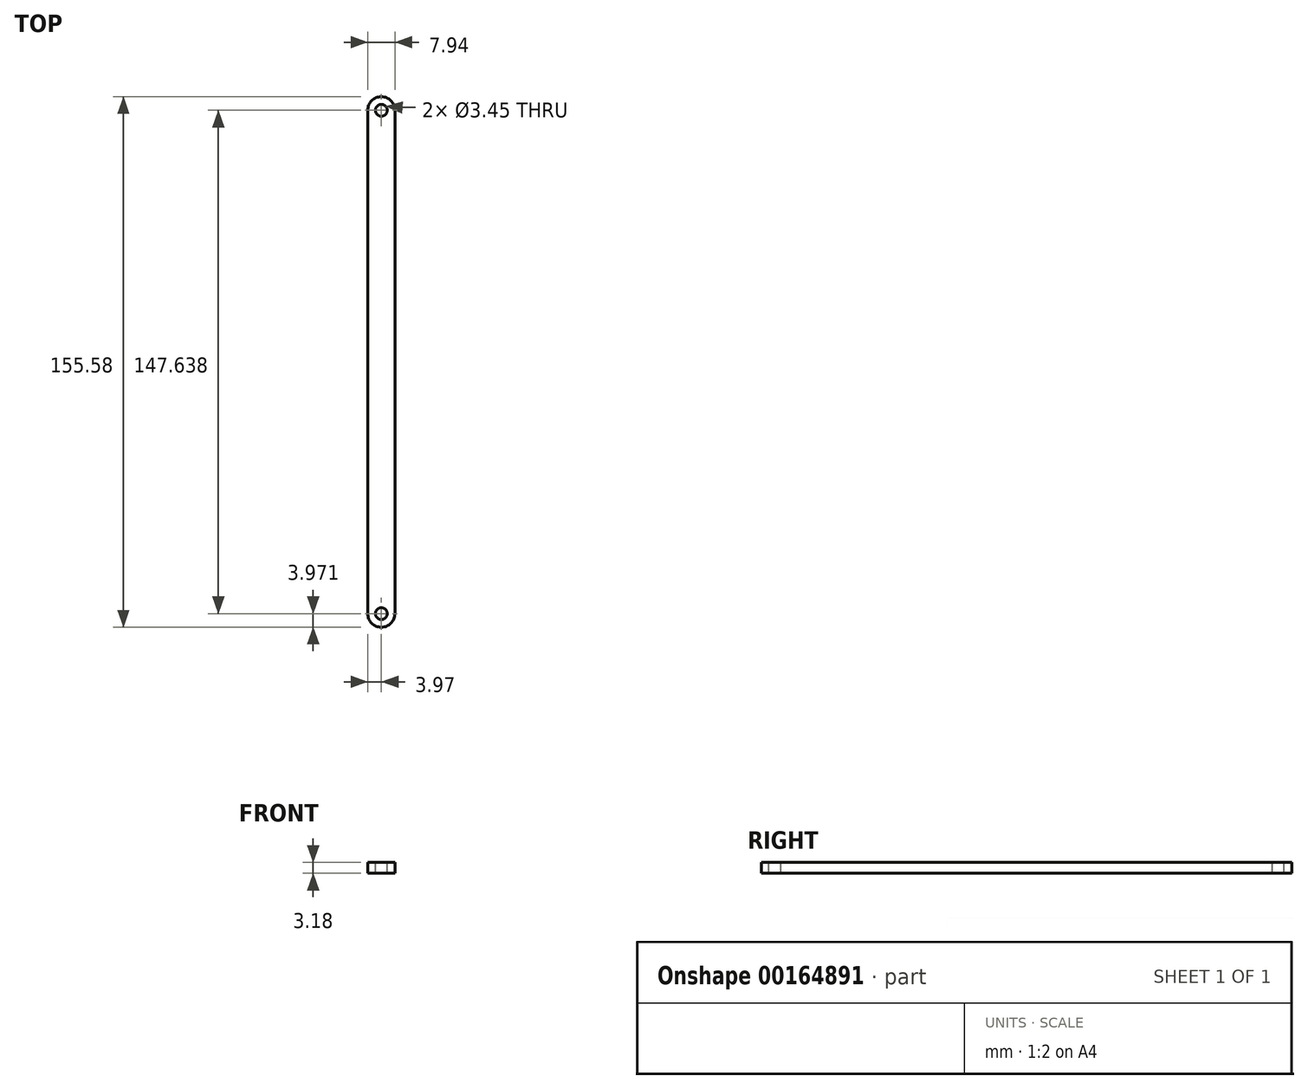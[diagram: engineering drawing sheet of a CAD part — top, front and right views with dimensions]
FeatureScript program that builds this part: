
annotation { "Feature Type Name" : "Feature", "Feature Type Description" : "" }
export const myFeature = defineFeature(function(context is Context, id is Id, definition is map)
    precondition{}
    {
        {
            var Q0;
            Q0=qCreatedBy(makeId("Top.planeOp"),FACE);
            var sketch = newSketch(context, id + "F0", { "sketchPlane" : qUnion([Q0])});
            skLineSegment(sketch, "E0.bottom", {"start": v(3.97, -77.79) * mm, "end": v(-3.97, -77.79) * mm});
            skLineSegment(sketch, "E0.top", {"start": v(3.97, 77.79) * mm, "end": v(-3.97, 77.79) * mm});
            skLineSegment(sketch, "E0.left", {"start": v(3.97, -77.79) * mm, "end": v(3.97, 77.79) * mm});
            skLineSegment(sketch, "E0.right", {"start": v(-3.97, -77.79) * mm, "end": v(-3.97, 77.79) * mm});
            skPoint(sketch, "E0.middle", {"position": v(0, 0) * mm});
            skSolve(sketch);
        }
        {
            var Q0;
            Q0=qSketchRegion(id+"F0",true);
            extrude(context, id + "F1", {"entities" : qUnion([Q0]), "depth" : 3.17 * mm});
        }
        {
            var Q0;
            Q0=makeQuery(id+"F1.opExtrude","CAP_FACE",FACE,{"disambiguationData":[OSD([sQuery(id+"F0.wireOp",EDGE,"E0.bottom"),sQuery(id+"F0.wireOp",EDGE,"E0.top"),sQuery(id+"F0.wireOp",EDGE,"E0.left"),sQuery(id+"F0.wireOp",EDGE,"E0.right"),sQuery(id+"F0.wireOp",EDGE,"RtZi68gI-vAEL-Mczj-9c6q-gRGCdm8V3NPa")])],"isStart":false});
            var sketch = newSketch(context, id + "F2", { "sketchPlane" : qUnion([Q0])});
            skLineSegment(sketch, "E1.bottom", {"start": v(0, 77.79) * mm, "end": v(3.97, 77.79) * mm, "construction": true});
            skLineSegment(sketch, "E1.top", {"start": v(0, 73.82) * mm, "end": v(3.97, 73.82) * mm, "construction": true});
            skLineSegment(sketch, "E1.left", {"start": v(0, 77.79) * mm, "end": v(0, 73.82) * mm, "construction": true});
            skLineSegment(sketch, "E1.right", {"start": v(3.97, 77.79) * mm, "end": v(3.97, 73.82) * mm, "construction": true});
            skLineSegment(sketch, "E2.bottom", {"start": v(0, -77.79) * mm, "end": v(3.97, -77.79) * mm, "construction": true});
            skLineSegment(sketch, "E2.top", {"start": v(0, -73.82) * mm, "end": v(3.97, -73.82) * mm, "construction": true});
            skLineSegment(sketch, "E2.left", {"start": v(0, -77.79) * mm, "end": v(0, -73.82) * mm, "construction": true});
            skLineSegment(sketch, "E2.right", {"start": v(3.97, -77.79) * mm, "end": v(3.97, -73.82) * mm, "construction": true});
            skCircle(sketch, "E3", {"center": v(0, 73.82) * mm, "radius": 1.73 * mm});
            skCircle(sketch, "E4", {"center": v(0, -73.82) * mm, "radius": 1.73 * mm});
            skSolve(sketch);
        }
        {
            var Q0;
            Q0=qSketchRegion(id+"F2",true);
            var Q1;
            Q1=makeQuery(id+"F1.opExtrude","CAP_FACE",FACE,{"disambiguationData":[OSD([sQuery(id+"F0.wireOp",EDGE,"E0.bottom"),sQuery(id+"F0.wireOp",EDGE,"E0.top"),sQuery(id+"F0.wireOp",EDGE,"E0.left"),sQuery(id+"F0.wireOp",EDGE,"E0.right"),sQuery(id+"F0.wireOp",EDGE,"RtZi68gI-vAEL-Mczj-9c6q-gRGCdm8V3NPa")])],"isStart":true});
            extrude(context, id + "F3", {"entities" : qUnion([Q0]), "operationType" : NewBodyOperationType.REMOVE, "endBound" : BoundingType.UP_TO_SURFACE, "oppositeDirection" : true, "endBoundEntityFace" : qUnion([Q1]), "depth" : 25.4 * mm});
        }
        {
            var Q0;
            Q0=makeQuery(id+"F1.opExtrude","SWEPT_EDGE",EDGE,{"disambiguationData":[OSD([sQuery(id+"F0.wireOp",EDGE,"E0.bottom"),sQuery(id+"F0.wireOp",EDGE,"E0.right")])]});
            var Q1;
            Q1=makeQuery(id+"F1.opExtrude","SWEPT_EDGE",EDGE,{"disambiguationData":[OSD([sQuery(id+"F0.wireOp",EDGE,"E0.bottom"),sQuery(id+"F0.wireOp",EDGE,"E0.left")])]});
            var Q2;
            Q2=makeQuery(id+"F1.opExtrude","SWEPT_EDGE",EDGE,{"disambiguationData":[OSD([sQuery(id+"F0.wireOp",EDGE,"E0.top"),sQuery(id+"F0.wireOp",EDGE,"E0.left")])]});
            var Q3;
            Q3=makeQuery(id+"F1.opExtrude","SWEPT_EDGE",EDGE,{"disambiguationData":[OSD([sQuery(id+"F0.wireOp",EDGE,"E0.top"),sQuery(id+"F0.wireOp",EDGE,"E0.right")])]});
            fillet(context, id + "F4", {"entities" : qUnion([Q0, Q1, Q2, Q3]), "radius" : 3.97 * mm, "tangentPropagation" : true, "allowEdgeOverflow" : false});
        }
    });
